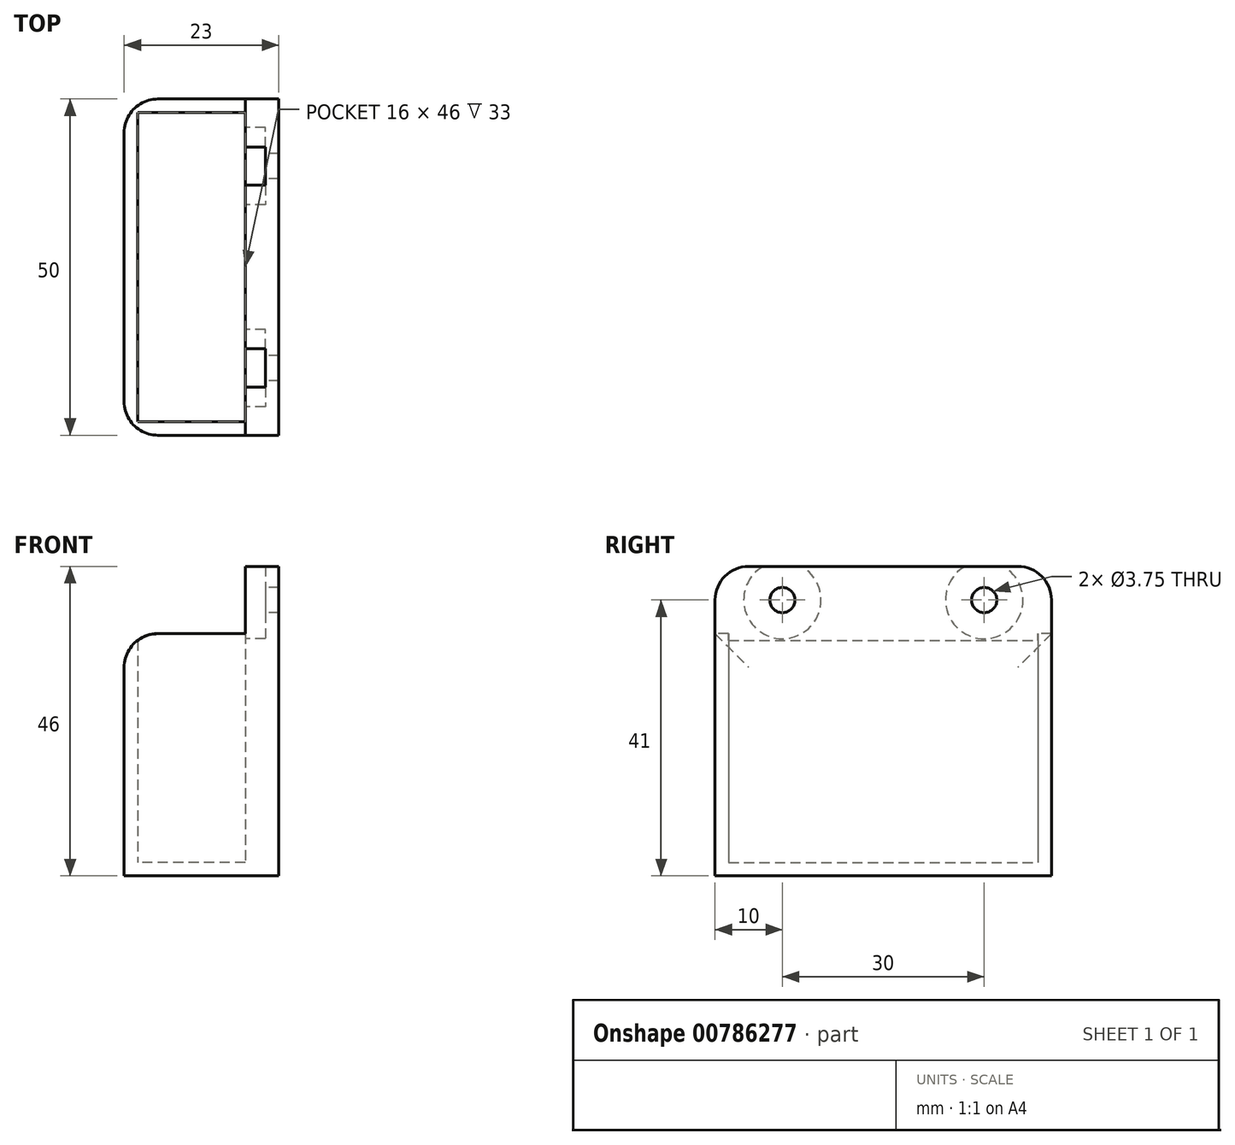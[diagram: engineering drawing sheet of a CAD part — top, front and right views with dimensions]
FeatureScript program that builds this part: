
annotation { "Feature Type Name" : "Feature", "Feature Type Description" : "" }
export const myFeature = defineFeature(function(context is Context, id is Id, definition is map)
    precondition{}
    {
        {
            var Q0;
            Q0=qCreatedBy(makeId("Top.planeOp"),FACE);
            var sketch = newSketch(context, id + "F0", { "sketchPlane" : qUnion([Q0])});
            skLineSegment(sketch, "E0.bottom", {"start": v(-8, 23) * mm, "end": v(8, 23) * mm});
            skLineSegment(sketch, "E0.top", {"start": v(-8, -23) * mm, "end": v(8, -23) * mm});
            skLineSegment(sketch, "E0.left", {"start": v(-8, 23) * mm, "end": v(-8, -23) * mm});
            skLineSegment(sketch, "E0.right", {"start": v(8, 23) * mm, "end": v(8, -23) * mm});
            skPoint(sketch, "E0.middle", {"position": v(0, 0) * mm});
            skLineSegment(sketch, "E1.0", {"start": v(-10, 25) * mm, "end": v(-10, -25) * mm});
            skLineSegment(sketch, "E1.1", {"start": v(-10, 25) * mm, "end": v(10, 25) * mm});
            skLineSegment(sketch, "E1.2", {"start": v(10, 25) * mm, "end": v(10, -25) * mm});
            skLineSegment(sketch, "E1.3", {"start": v(-10, -25) * mm, "end": v(10, -25) * mm});
            skSolve(sketch);
        }
        {
            var Q0;
            Q0=makeQuery(id+"F0.imprint","IMPRINT",FACE,{"disambiguationData":[TD([[makeQuery(id+"F0.imprint","IMPRINT",EDGE,{"derivedFrom":sQuery(id+"F0.wireOp",EDGE,"E0.bottom")}),-1.0]])]});
            var Q1;
            Q1=makeQuery(id+"F0.imprint","IMPRINT",FACE,{"disambiguationData":[TD([[makeQuery(id+"F0.imprint","IMPRINT",EDGE,{"derivedFrom":sQuery(id+"F0.wireOp",EDGE,"E0.bottom")}),1.0]])]});
            extrude(context, id + "F1", {"entities" : qUnion([Q0, Q1]), "depth" : 2 * mm, "offsetDistance" : 25 * mm});
        }
        {
            var Q0;
            Q0=makeQuery(id+"F0.imprint","IMPRINT",FACE,{"disambiguationData":[TD([[makeQuery(id+"F0.imprint","IMPRINT",EDGE,{"derivedFrom":sQuery(id+"F0.wireOp",EDGE,"E0.bottom")}),1.0]])]});
            extrude(context, id + "F2", {"entities" : qUnion([Q0]), "operationType" : NewBodyOperationType.ADD, "depth" : 36 * mm, "offsetDistance" : 25 * mm});
        }
        {
            var Q0;
            Q0=makeQuery(id+"F2.opExtrude","CAP_FACE",FACE,{"disambiguationData":[OSD([sQuery(id+"F0.wireOp",EDGE,"E0.bottom"),sQuery(id+"F0.wireOp",EDGE,"E0.top"),sQuery(id+"F0.wireOp",EDGE,"E0.left"),sQuery(id+"F0.wireOp",EDGE,"E0.right"),sQuery(id+"F0.wireOp",EDGE,"E1.0"),sQuery(id+"F0.wireOp",EDGE,"E1.1"),sQuery(id+"F0.wireOp",EDGE,"E1.2"),sQuery(id+"F0.wireOp",EDGE,"E1.3")])],"isStart":false});
            var sketch = newSketch(context, id + "F3", { "sketchPlane" : qUnion([Q0])});
            skLineSegment(sketch, "E2.bottom", {"start": v(10, 25) * mm, "end": v(8, 25) * mm});
            skLineSegment(sketch, "E2.top", {"start": v(10, -25) * mm, "end": v(8, -25) * mm});
            skLineSegment(sketch, "E2.left", {"start": v(10, 25) * mm, "end": v(10, -25) * mm});
            skLineSegment(sketch, "E2.right", {"start": v(8, 25) * mm, "end": v(8, -25) * mm});
            skSolve(sketch);
        }
        {
            var Q0;
            {var subQ2=sQuery(id+"F3.wireOp",EDGE,"E2.bottom");Q0=makeQuery(id+"F3.imprint","IMPRINT",FACE,{"disambiguationData":[TD([[makeQuery(id+"F3.imprint","IMPRINT",EDGE,{"derivedFrom":subQ2}),-1.0]])]});}
            extrude(context, id + "F4", {"entities" : qUnion([Q0]), "operationType" : NewBodyOperationType.ADD, "depth" : 10 * mm, "offsetDistance" : 25 * mm});
        }
        {
            var Q0;
            Q0=makeQuery(id+"F4.boolean.opBoolean","MERGE",FACE,{"derivedFrom":[makeQuery(id+"F2.opExtrude","SWEPT_FACE",FACE,{"disambiguationData":[OSD([sQuery(id+"F0.wireOp",EDGE,"E0.right")])]}),makeQuery(id+"F4.opExtrude","SWEPT_FACE",FACE,{"disambiguationData":[OSD([sQuery(id+"F3.wireOp",EDGE,"E2.right")])]})]});
            var sketch = newSketch(context, id + "F5", { "sketchPlane" : qUnion([Q0])});
            skLineSegment(sketch, "E3", {"start": v(0, 46) * mm, "end": v(0, 41) * mm, "construction": true});
            skLineSegment(sketch, "E4", {"start": v(0, 41) * mm, "end": v(15, 41) * mm, "construction": true});
            skLineSegment(sketch, "E5", {"start": v(0, 41) * mm, "end": v(-15, 41) * mm, "construction": true});
            skCircle(sketch, "E6", {"center": v(-15, 41) * mm, "radius": 1.88 * mm});
            skCircle(sketch, "E7", {"center": v(15, 41) * mm, "radius": 1.88 * mm});
            skCircle(sketch, "E8", {"center": v(15, 41) * mm, "radius": 5.75 * mm});
            skCircle(sketch, "E9", {"center": v(-15, 41) * mm, "radius": 5.75 * mm});
            skSolve(sketch);
        }
        {
            var Q0;
            Q0=makeQuery(id+"F5.imprint","IMPRINT",FACE,{"disambiguationData":[TD([[makeQuery(id+"F5.imprint","IMPRINT",EDGE,{"derivedFrom":sQuery(id+"F5.wireOp",EDGE,"E7")}),1.0]])]});
            var Q1;
            Q1=makeQuery(id+"F5.imprint","IMPRINT",FACE,{"disambiguationData":[TD([[makeQuery(id+"F5.imprint","IMPRINT",EDGE,{"derivedFrom":sQuery(id+"F5.wireOp",EDGE,"E6")}),1.0]])]});
            extrude(context, id + "F6", {"entities" : qUnion([Q0, Q1]), "operationType" : NewBodyOperationType.REMOVE, "oppositeDirection" : true, "depth" : 25 * mm, "offsetDistance" : 25 * mm});
        }
        {
            var Q0;
            {var subQ0=sQuery(id+"F0.wireOp",EDGE,"E1.3");var subQ1=sQuery(id+"F0.wireOp",EDGE,"E1.0");Q0=makeQuery(id+"F2.boolean.opBoolean","MERGE",EDGE,{"derivedFrom":[makeQuery(id+"F1.opExtrude","SWEPT_EDGE",EDGE,{"disambiguationData":[OSD([subQ1,subQ0])]}),makeQuery(id+"F2.opExtrude","SWEPT_EDGE",EDGE,{"disambiguationData":[OSD([subQ1,subQ0])]})]});}
            var Q1;
            {var subQ0=sQuery(id+"F0.wireOp",EDGE,"E1.1");var subQ1=sQuery(id+"F0.wireOp",EDGE,"E1.0");Q1=makeQuery(id+"F2.boolean.opBoolean","MERGE",EDGE,{"derivedFrom":[makeQuery(id+"F1.opExtrude","SWEPT_EDGE",EDGE,{"disambiguationData":[OSD([subQ1,subQ0])]}),makeQuery(id+"F2.opExtrude","SWEPT_EDGE",EDGE,{"disambiguationData":[OSD([subQ1,subQ0])]})]});}
            var Q2;
            Q2=makeQuery(id+"F4.opExtrude","CAP_EDGE",EDGE,{"disambiguationData":[OSD([sQuery(id+"F3.wireOp",EDGE,"E2.top")])],"isStart":false});
            var Q3;
            Q3=makeQuery(id+"F4.opExtrude","CAP_EDGE",EDGE,{"disambiguationData":[OSD([sQuery(id+"F3.wireOp",EDGE,"E2.bottom")])],"isStart":false});
            var Q4;
            {var subQ2=sQuery(id+"F0.wireOp",EDGE,"E1.3");var subQ3=sQuery(id+"F3.wireOp",EDGE,"E2.right");Q4=makeQuery(id+"F4.boolean.opBoolean","SPLIT",EDGE,{"disambiguationData":[TD([makeQuery(id+"F1.opExtrude","SWEPT_FACE",FACE,{"disambiguationData":[OSD([subQ2])]})])],"derivedFrom":makeQuery(id+"F4.opExtrude","CAP_EDGE",EDGE,{"disambiguationData":[OSD([subQ3])],"isStart":true})});}
            var Q5;
            {var subQ2=sQuery(id+"F0.wireOp",EDGE,"E1.1");var subQ3=sQuery(id+"F3.wireOp",EDGE,"E2.right");Q5=makeQuery(id+"F4.boolean.opBoolean","SPLIT",EDGE,{"disambiguationData":[TD([makeQuery(id+"F1.opExtrude","SWEPT_FACE",FACE,{"disambiguationData":[OSD([subQ2])]})])],"derivedFrom":makeQuery(id+"F4.opExtrude","CAP_EDGE",EDGE,{"disambiguationData":[OSD([subQ3])],"isStart":true})});}
            var Q6;
            Q6=makeQuery(id+"F2.opExtrude","CAP_EDGE",EDGE,{"disambiguationData":[OSD([sQuery(id+"F0.wireOp",EDGE,"E1.0")])],"isStart":false});
            fillet(context, id + "F7", {"entities" : qUnion([Q0, Q1, Q2, Q3, Q4, Q5, Q6]), "radius" : 5 * mm, "tangentPropagation" : true, "allowEdgeOverflow" : false});
        }
        {
            var Q0;
            {var subQ0=sQuery(id+"F0.wireOp",EDGE,"E1.2");Q0=makeQuery(id+"F4.boolean.opBoolean","MERGE",FACE,{"derivedFrom":[makeQuery(id+"F2.boolean.opBoolean","MERGE",FACE,{"derivedFrom":[makeQuery(id+"F1.opExtrude","SWEPT_FACE",FACE,{"disambiguationData":[OSD([subQ0])]}),makeQuery(id+"F2.opExtrude","SWEPT_FACE",FACE,{"disambiguationData":[OSD([subQ0])]})]}),makeQuery(id+"F4.opExtrude","SWEPT_FACE",FACE,{"disambiguationData":[OSD([sQuery(id+"F3.wireOp",EDGE,"E2.left")])]})]});}
            extrude(context, id + "F8", {"entities" : qUnion([Q0]), "operationType" : NewBodyOperationType.ADD, "depth" : 3 * mm, "offsetDistance" : 25 * mm});
        }
        {
            var Q0;
            Q0=makeQuery(id+"F5.imprint","IMPRINT",FACE,{"disambiguationData":[TD([[makeQuery(id+"F5.imprint","IMPRINT",EDGE,{"derivedFrom":sQuery(id+"F5.wireOp",EDGE,"E6")}),-1.0]])]});
            var Q1;
            Q1=makeQuery(id+"F5.imprint","IMPRINT",FACE,{"disambiguationData":[TD([[makeQuery(id+"F5.imprint","IMPRINT",EDGE,{"derivedFrom":sQuery(id+"F5.wireOp",EDGE,"E7")}),-1.0]])]});
            extrude(context, id + "F9", {"entities" : qUnion([Q0, Q1]), "operationType" : NewBodyOperationType.REMOVE, "oppositeDirection" : true, "depth" : 3 * mm, "offsetDistance" : 25 * mm});
        }
    });
